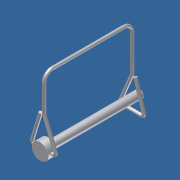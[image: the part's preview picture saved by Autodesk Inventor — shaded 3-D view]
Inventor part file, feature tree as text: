
AUTODESK INVENTOR PART (.ipt)
format: ipt  version: 2011 (Build 150239000, 239)  size: 169,472 bytes
history: native  units: in
note: dims shown in document units (in); Inventor stores cm internally (conversion verified against a paired STEP export)
features: sketch x6, plane x4, extrude x2, fillet x1, chamfer x1, sweep x1, other x1, projected_geometry x1
ambient origin geometry x8: Origin, YZ Plane, XZ Plane, XY Plane, X Axis, Y Axis, Z Axis, Center Point
bodies: Solid1 (feature_tree)
feature tree (17):
  sketch  "Sketch1"  dims[d6=0.495in d8=0.25in d9=0.0in d10=0.01in]
  extrude  "Extrusion1"  Depth=0.25in TaperAngle=0.0deg
  fillet  "Fillet1"  Radius=0.01in
  extrude  "Extrusion2"  Depth=2.75in TaperAngle=0.0deg
  chamfer  "Chamfer1"  Distance=0.025in Angle=45.0deg
  plane  "Work Plane1"
  sketch  "Sketch2"  dims[d11=0.245in d12=2.75in d13=0.0in d14=0.025in d15=0.125in d16=45.0deg]
  plane  "Work Plane2"
  sketch  "Sketch3"  dims[d17=0.0in d18=0.125in]
  sketch  "Sketch4"  dims[d19=0.095in]
  plane  "Work Plane3"
  sketch  "Sketch5"  dims[d20=-0.125in]
  plane  "Work Plane4"
  sweep  "Sweep1"
  other  "Work Axis1"
  projected_geometry  "Projected Loop1"
  sketch  "Sketch6"  dims[d21=0.75in d22=0.9in d23=0.9in d24=0.375in d25=0.1in d26=0.06in d27=1.715in d28=0.25in d29=0.25in d31=0.25in d32=2.625in d33=2.015in d34=0.75in d35=0.375in d36=0.1in d37=0.9in d38=0.9in d39=0.06in d40=0.06in d41=0.095in d42=0.0in]
